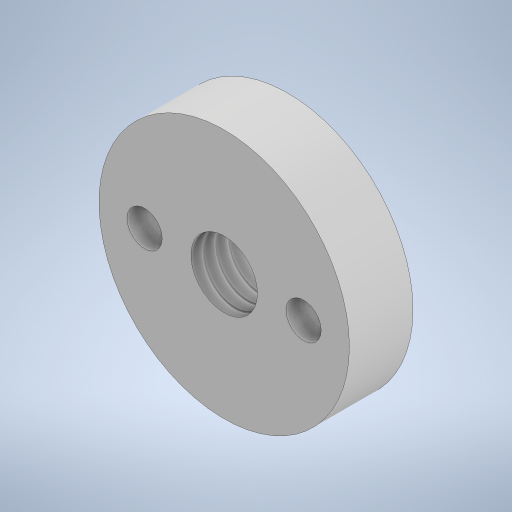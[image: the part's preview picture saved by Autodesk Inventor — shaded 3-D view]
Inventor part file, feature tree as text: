
AUTODESK INVENTOR PART (.ipt)
format: ipt  version: 2024 (Build 280153000, 153)  size: 231,936 bytes
history: native  units: mm
features: sketch x3, hole x2, extrude x1
ambient origin geometry x8: Origin, YZ Plane, XZ Plane, XY Plane, X Axis, Y Axis, Z Axis, Center Point
bodies: Solid1 (feature_tree)
feature tree (6):
  extrude  "Extrusion1"  Depth=6.35mm TaperAngle=0.0deg
  hole  "Hole1"  [1 undecoded]
  hole  "Hole2"  [1 undecoded]
  sketch  "Sketch1"  dims[d0=25.0mm d1=6.35mm d2=0.0mm]
  sketch  "Sketch2"  dims[d3=6.647mm d4=16.0mm d5=4.0mm d6=2.0mm d7=90.0deg d8=8.0mm d9=20.594885mm d10=15.875mm]
  sketch  "Sketch3"  dims[d11=3.5mm d12=3.5mm d13=4.0mm d14=2.0mm d15=90.0deg d16=8.0mm d17=20.594885mm]
note: 2 required parameter values undecoded (feature->parameter linkage not recoverable at this tier; creation-order binding heuristic only, values carry confidence <= 0.55)
